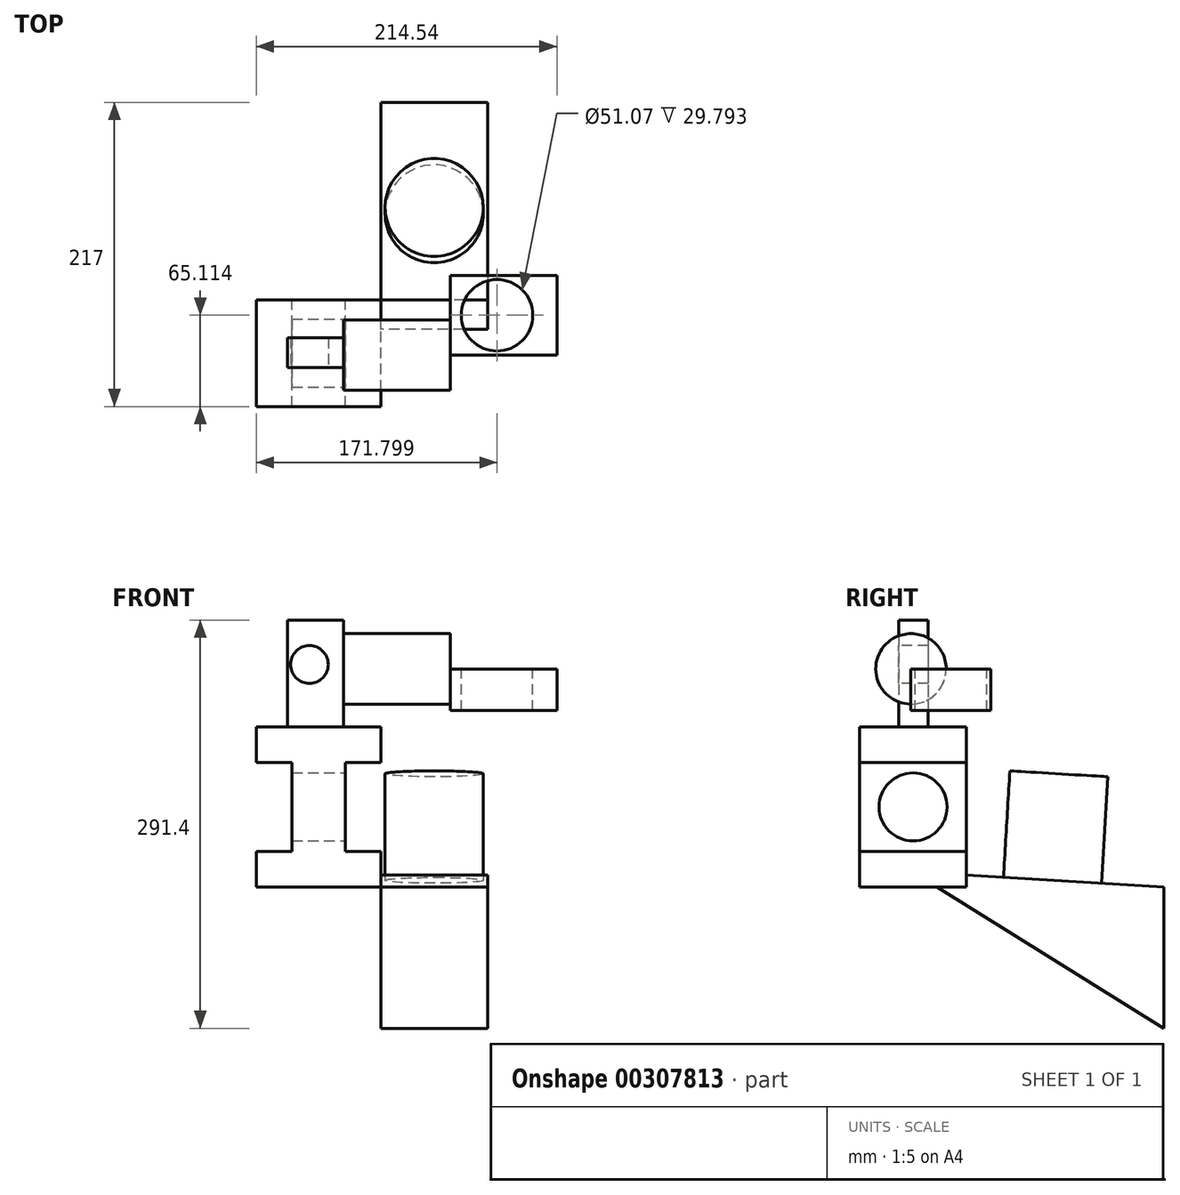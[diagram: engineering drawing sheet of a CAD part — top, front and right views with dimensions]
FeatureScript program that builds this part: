
annotation { "Feature Type Name" : "Feature", "Feature Type Description" : "" }
export const myFeature = defineFeature(function(context is Context, id is Id, definition is map)
    precondition{}
    {
        {
            var Q0;
            Q0=qCreatedBy(makeId("Front.planeOp"),FACE);
            var sketch = newSketch(context, id + "F0", { "sketchPlane" : qUnion([Q0])});
            skLineSegment(sketch, "E0", {"start": v(-43.77, -50.04) * mm, "end": v(45.13, -50.04) * mm});
            skLineSegment(sketch, "E1", {"start": v(45.13, -50.04) * mm, "end": v(45.13, -24.64) * mm});
            skLineSegment(sketch, "E2", {"start": v(19.73, -24.64) * mm, "end": v(45.13, -24.64) * mm});
            skLineSegment(sketch, "E3", {"start": v(19.73, 38.86) * mm, "end": v(19.73, -24.64) * mm});
            skLineSegment(sketch, "E4", {"start": v(19.73, 38.86) * mm, "end": v(45.13, 38.86) * mm});
            skLineSegment(sketch, "E5", {"start": v(45.13, 38.86) * mm, "end": v(45.13, 64.26) * mm});
            skLineSegment(sketch, "E6", {"start": v(45.13, 64.26) * mm, "end": v(-43.77, 64.26) * mm});
            skLineSegment(sketch, "E7", {"start": v(-43.77, 64.26) * mm, "end": v(-43.77, 38.86) * mm});
            skLineSegment(sketch, "E8", {"start": v(-43.77, 38.86) * mm, "end": v(-18.37, 38.86) * mm});
            skLineSegment(sketch, "E9", {"start": v(-18.37, 38.86) * mm, "end": v(-18.37, -24.64) * mm});
            skLineSegment(sketch, "E10", {"start": v(-18.37, -24.64) * mm, "end": v(-43.77, -24.64) * mm});
            skLineSegment(sketch, "E11", {"start": v(-43.77, -24.64) * mm, "end": v(-43.77, -50.04) * mm});
            skSolve(sketch);
        }
        {
            var Q0;
            Q0=makeQuery(id+"F0.imprint","IMPRINT",FACE,{"disambiguationData":[TD([[makeQuery(id+"F0.imprint","IMPRINT",EDGE,{"derivedFrom":sQuery(id+"F0.wireOp",EDGE,"E0")}),1.0]])]});
            extrude(context, id + "F1", {"entities" : qUnion([Q0]), "depth" : 76.2 * mm});
        }
        {
            var Q0;
            Q0=makeQuery(id+"F1.opExtrude","SWEPT_FACE",FACE,{"disambiguationData":[OSD([sQuery(id+"F0.wireOp",EDGE,"E3")])]});
            var sketch = newSketch(context, id + "F2", { "sketchPlane" : qUnion([Q0])});
            skCircle(sketch, "E12", {"center": v(-38.1, 7.1) * mm, "radius": 24.26 * mm});
            skPoint(sketch, "E12.centerSnap0", {"position": v(-38.1, 38.86) * mm});
            skPoint(sketch, "E12.centerSnap1", {"position": v(-76.2, 7.1) * mm});
            skSolve(sketch);
        }
        {
            var Q0;
            Q0=makeQuery(id+"F2.imprint","IMPRINT",FACE,{"disambiguationData":[TD([[makeQuery(id+"F2.imprint","IMPRINT",EDGE,{"derivedFrom":sQuery(id+"F2.wireOp",EDGE,"E12")}),1.0]])]});
            extrude(context, id + "F3", {"entities" : qUnion([Q0]), "operationType" : NewBodyOperationType.REMOVE, "endBound" : BoundingType.THROUGH_ALL, "oppositeDirection" : true, "depth" : 25.4 * mm});
        }
        {
            var Q0;
            Q0=makeQuery(id+"F1.opExtrude","SWEPT_FACE",FACE,{"disambiguationData":[OSD([sQuery(id+"F0.wireOp",EDGE,"E6")])]});
            var sketch = newSketch(context, id + "F4", { "sketchPlane" : qUnion([Q0])});
            skLineSegment(sketch, "E13", {"start": v(-21.56, -27.23) * mm, "end": v(18.37, -27.23) * mm});
            skLineSegment(sketch, "E14", {"start": v(18.37, -27.23) * mm, "end": v(18.37, -48.46) * mm});
            skLineSegment(sketch, "E15", {"start": v(18.37, -48.46) * mm, "end": v(-21.56, -48.46) * mm});
            skLineSegment(sketch, "E16", {"start": v(-21.56, -48.46) * mm, "end": v(-21.56, -27.23) * mm});
            skSolve(sketch);
        }
        {
            var Q0;
            Q0=makeQuery(id+"F4.imprint","IMPRINT",FACE,{"disambiguationData":[TD([[makeQuery(id+"F4.imprint","IMPRINT",EDGE,{"derivedFrom":sQuery(id+"F4.wireOp",EDGE,"E13")}),-1.0]])]});
            extrude(context, id + "F5", {"entities" : qUnion([Q0]), "operationType" : NewBodyOperationType.ADD, "depth" : 76.2 * mm});
        }
        {
            var Q0;
            Q0=makeQuery(id+"F5.opExtrude","SWEPT_FACE",FACE,{"disambiguationData":[OSD([sQuery(id+"F4.wireOp",EDGE,"E15")])]});
            var sketch = newSketch(context, id + "F6", { "sketchPlane" : qUnion([Q0])});
            skCircle(sketch, "E17", {"center": v(-5.88, 108.79) * mm, "radius": 13.46 * mm});
            skSolve(sketch);
        }
        {
            var Q0;
            Q0=makeQuery(id+"F6.imprint","IMPRINT",FACE,{"disambiguationData":[TD([[makeQuery(id+"F6.imprint","IMPRINT",EDGE,{"derivedFrom":sQuery(id+"F6.wireOp",EDGE,"E17")}),1.0]])]});
            extrude(context, id + "F7", {"entities" : qUnion([Q0]), "operationType" : NewBodyOperationType.REMOVE, "endBound" : BoundingType.THROUGH_ALL, "oppositeDirection" : true, "depth" : 25.4 * mm});
        }
        {
            var Q0;
            Q0=makeQuery(id+"F5.opExtrude","SWEPT_FACE",FACE,{"disambiguationData":[OSD([sQuery(id+"F4.wireOp",EDGE,"E14")])]});
            var sketch = newSketch(context, id + "F8", { "sketchPlane" : qUnion([Q0])});
            skCircle(sketch, "E18", {"center": v(-39.62, 105.62) * mm, "radius": 25.14 * mm});
            skSolve(sketch);
        }
        {
            var Q0;
            {var subQ0=sQuery(id+"F8.wireOp",EDGE,"E18");var subQ1=makeQuery(id+"F5.opExtrude","SWEPT_EDGE",EDGE,{"disambiguationData":[OSD([sQuery(id+"F4.wireOp",EDGE,"E14"),sQuery(id+"F4.wireOp",EDGE,"E15")])]});var subQ2=makeQuery(id+"F8.imprint","INTERSECT",VERTEX,{"disambiguationData":[OD(0.0)],"derivedFrom":[subQ1,subQ0]});Q0=makeQuery(id+"F8.imprint","IMPRINT",FACE,{"disambiguationData":[TD([[makeQuery(id+"F8.imprint","IMPRINT",EDGE,{"disambiguationData":[TD([[subQ2,-1.0]])],"derivedFrom":subQ0}),1.0]])]});}
            var Q1;
            {var subQ0=sQuery(id+"F8.wireOp",EDGE,"E18");var subQ1=makeQuery(id+"F5.opExtrude","SWEPT_EDGE",EDGE,{"disambiguationData":[OSD([sQuery(id+"F4.wireOp",EDGE,"E13"),sQuery(id+"F4.wireOp",EDGE,"E14")])]});var subQ2=makeQuery(id+"F8.imprint","INTERSECT",VERTEX,{"disambiguationData":[OD(0.0)],"derivedFrom":[subQ1,subQ0]});Q1=makeQuery(id+"F8.imprint","IMPRINT",FACE,{"disambiguationData":[TD([[makeQuery(id+"F8.imprint","IMPRINT",EDGE,{"disambiguationData":[TD([[subQ2,1.0]])],"derivedFrom":subQ0}),1.0]])]});}
            var Q2;
            {var subQ0=sQuery(id+"F8.wireOp",EDGE,"E18");var subQ1=sQuery(id+"F4.wireOp",EDGE,"E14");var subQ2=makeQuery(id+"F5.opExtrude","SWEPT_EDGE",EDGE,{"disambiguationData":[OSD([subQ1,sQuery(id+"F4.wireOp",EDGE,"E15")])]});var subQ3=makeQuery(id+"F8.imprint","INTERSECT",VERTEX,{"disambiguationData":[OD(0.0)],"derivedFrom":[subQ2,subQ0]});Q2=makeQuery(id+"F8.imprint","IMPRINT",FACE,{"disambiguationData":[TD([[makeQuery(id+"F8.imprint","IMPRINT",EDGE,{"disambiguationData":[TD([[subQ3,1.0]])],"derivedFrom":subQ0}),1.0]])]});}
            extrude(context, id + "F9", {"entities" : qUnion([Q0, Q1, Q2]), "operationType" : NewBodyOperationType.ADD, "depth" : 76.2 * mm});
        }
        {
            var Q0;
            Q0=makeQuery(id+"F9.opExtrude","CAP_FACE",FACE,{"disambiguationData":[OSD([sQuery(id+"F8.wireOp",EDGE,"E18")])],"isStart":false});
            var sketch = newSketch(context, id + "F10", { "sketchPlane" : qUnion([Q0])});
            skLineSegment(sketch, "E19", {"start": v(-39.62, 105.62) * mm, "end": v(17.45, 105.62) * mm});
            skLineSegment(sketch, "E20", {"start": v(17.45, 105.62) * mm, "end": v(17.45, 75.82) * mm});
            skLineSegment(sketch, "E21", {"start": v(17.45, 75.82) * mm, "end": v(-39.62, 75.82) * mm});
            skLineSegment(sketch, "E22", {"start": v(-39.62, 75.82) * mm, "end": v(-39.62, 105.62) * mm});
            skSolve(sketch);
        }
        {
            var Q0;
            {var subQ4=sQuery(id+"F10.wireOp",EDGE,"E20");Q0=makeQuery(id+"F10.imprint","IMPRINT",FACE,{"disambiguationData":[TD([[makeQuery(id+"F10.imprint","IMPRINT",EDGE,{"derivedFrom":subQ4}),-1.0]])]});}
            var Q1;
            {var subQ0=sQuery(id+"F10.wireOp",EDGE,"E22");var subQ1=sQuery(id+"F10.wireOp",EDGE,"E19");var subQ2=makeQuery(id+"F10.imprint","INTERSECT",VERTEX,{"derivedFrom":[subQ1,subQ0]});Q1=makeQuery(id+"F10.imprint","IMPRINT",FACE,{"disambiguationData":[TD([[makeQuery(id+"F10.imprint","IMPRINT",EDGE,{"disambiguationData":[TD([[subQ2,-1.0]])],"derivedFrom":subQ1}),-1.0]])]});}
            extrude(context, id + "F11", {"entities" : qUnion([Q0, Q1]), "operationType" : NewBodyOperationType.ADD, "depth" : 76.2 * mm});
        }
        {
            var Q0;
            Q0=makeQuery(id+"F11.opExtrude","SWEPT_FACE",FACE,{"disambiguationData":[OSD([sQuery(id+"F10.wireOp",EDGE,"E19")])]});
            var sketch = newSketch(context, id + "F12", { "sketchPlane" : qUnion([Q0])});
            skCircle(sketch, "E23", {"center": v(128.03, -11.09) * mm, "radius": 25.53 * mm});
            skPoint(sketch, "E23.centerSnap0", {"position": v(170.77, -11.09) * mm});
            skSolve(sketch);
        }
        {
            var Q0;
            Q0=makeQuery(id+"F12.imprint","IMPRINT",FACE,{"disambiguationData":[TD([[makeQuery(id+"F12.imprint","IMPRINT",EDGE,{"derivedFrom":sQuery(id+"F12.wireOp",EDGE,"E23")}),1.0]])]});
            extrude(context, id + "F13", {"entities" : qUnion([Q0]), "operationType" : NewBodyOperationType.REMOVE, "endBound" : BoundingType.THROUGH_ALL, "oppositeDirection" : true, "depth" : 25.4 * mm});
        }
        {
            var Q0;
            Q0=makeQuery(id+"F1.opExtrude","SWEPT_FACE",FACE,{"disambiguationData":[OSD([sQuery(id+"F0.wireOp",EDGE,"E1")])]});
            var sketch = newSketch(context, id + "F14", { "sketchPlane" : qUnion([Q0])});
            skLineSegment(sketch, "E24", {"start": v(-38.1, -39.38) * mm, "end": v(140.8, -150.94) * mm});
            skPoint(sketch, "E24.startSnap0", {"position": v(-38.1, -50.04) * mm});
            skLineSegment(sketch, "E25", {"start": v(140.8, -150.94) * mm, "end": v(140.8, -50.04) * mm});
            skLineSegment(sketch, "E26", {"start": v(140.8, -50.04) * mm, "end": v(-38.1, -39.38) * mm});
            skSolve(sketch);
        }
        {
            var Q0;
            {var subQ7=sQuery(id+"F14.wireOp",EDGE,"E25");Q0=makeQuery(id+"F14.imprint","IMPRINT",FACE,{"disambiguationData":[TD([[makeQuery(id+"F14.imprint","IMPRINT",EDGE,{"derivedFrom":subQ7}),1.0]])]});}
            extrude(context, id + "F15", {"entities" : qUnion([Q0]), "depth" : 76.2 * mm});
        }
        {
            var Q0;
            Q0=makeQuery(id+"F15.opExtrude","SWEPT_FACE",FACE,{"disambiguationData":[OSD([sQuery(id+"F14.wireOp",EDGE,"E26")])]});
            var sketch = newSketch(context, id + "F16", { "sketchPlane" : qUnion([Q0])});
            skCircle(sketch, "E27", {"center": v(83.14, 63.95) * mm, "radius": 35 * mm});
            skSolve(sketch);
        }
        {
            var Q0;
            Q0=makeQuery(id+"F16.imprint","IMPRINT",FACE,{"disambiguationData":[TD([[makeQuery(id+"F16.imprint","IMPRINT",EDGE,{"derivedFrom":sQuery(id+"F16.wireOp",EDGE,"E27")}),1.0]])]});
            extrude(context, id + "F17", {"entities" : qUnion([Q0]), "operationType" : NewBodyOperationType.ADD, "depth" : 76.2 * mm});
        }
    });
